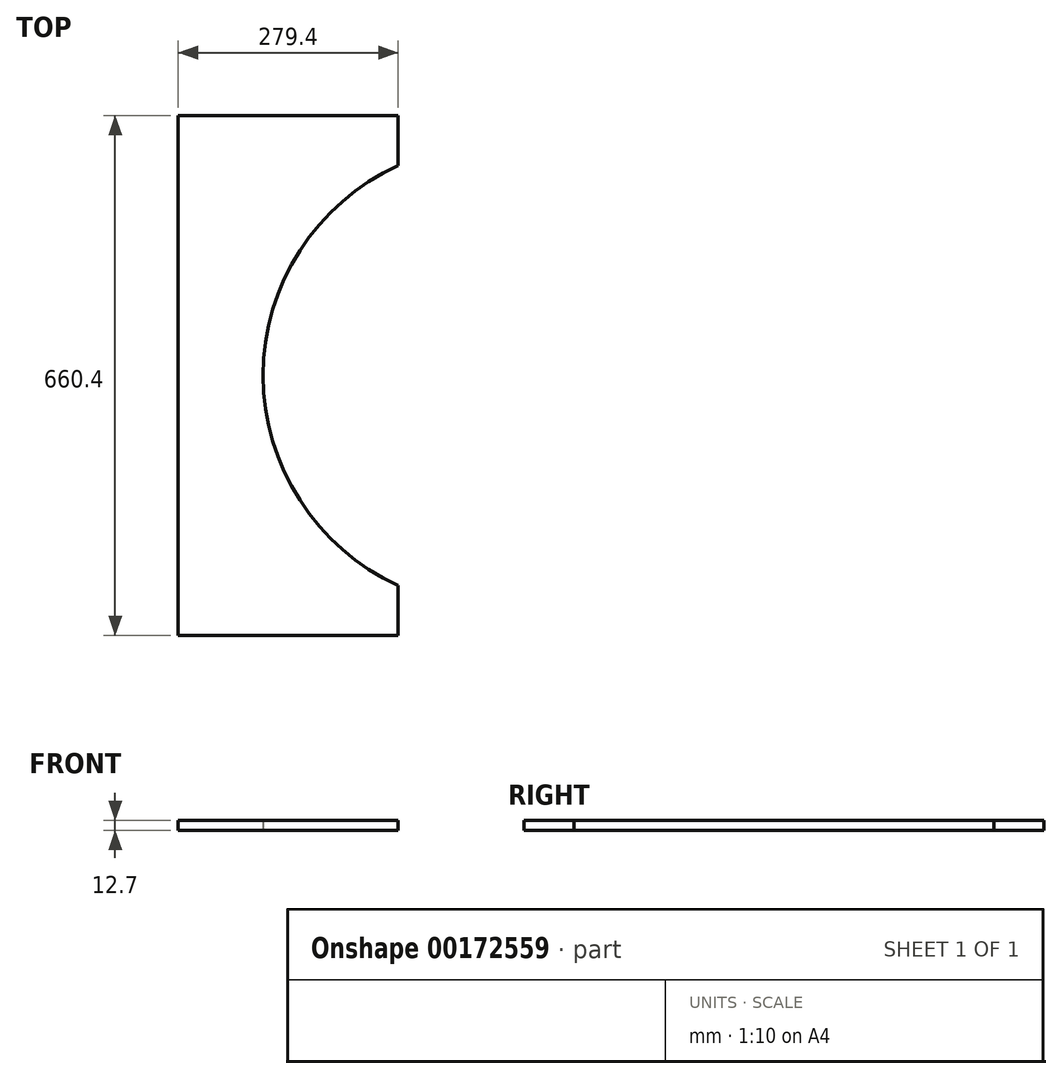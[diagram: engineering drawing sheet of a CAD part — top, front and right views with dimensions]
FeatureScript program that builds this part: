
annotation { "Feature Type Name" : "Feature", "Feature Type Description" : "" }
export const myFeature = defineFeature(function(context is Context, id is Id, definition is map)
    precondition{}
    {
        {
            var Q0;
            Q0=qCreatedBy(makeId("Top.planeOp"),FACE);
            var sketch = newSketch(context, id + "F0", { "sketchPlane" : qUnion([Q0])});
            skLineSegment(sketch, "E0", {"start": v(0, 0) * mm, "end": v(0, 330.2) * mm});
            skLineSegment(sketch, "E1", {"start": v(0, 0) * mm, "end": v(0, -330.2) * mm});
            skLineSegment(sketch, "E2", {"start": v(0, 330.2) * mm, "end": v(279.4, 330.2) * mm});
            skLineSegment(sketch, "E3", {"start": v(0, -330.2) * mm, "end": v(279.4, -330.2) * mm});
            skLineSegment(sketch, "E4", {"start": v(279.4, 330.2) * mm, "end": v(279.4, 266.7) * mm});
            skLineSegment(sketch, "E5", {"start": v(279.4, -330.2) * mm, "end": v(279.4, -266.7) * mm});
            skArc(sketch, "E6", {"start": v(279.4, 266.7) * mm, "mid": v(107.95, 0) * mm, "end": v(279.4, -266.7) * mm});
            skLineSegment(sketch, "E7", {"start": v(0, 0) * mm, "end": v(406.4, 0) * mm, "construction": true});
            skPoint(sketch, "E7.endSnap0", {"position": v(107.95, 0) * mm});
            skLineSegment(sketch, "E8", {"start": v(279.4, -266.7) * mm, "end": v(401.1, 0) * mm, "construction": true});
            skLineSegment(sketch, "E9", {"start": v(279.4, 266.7) * mm, "end": v(401.1, 0) * mm, "construction": true});
            skSolve(sketch);
        }
        {
            var Q0;
            Q0 = qSketchRegion(id + "F0", true);
            extrude(context, id + "F1", {"entities" : qUnion([Q0]), "depth" : 12.7 * mm});
        }
    });
